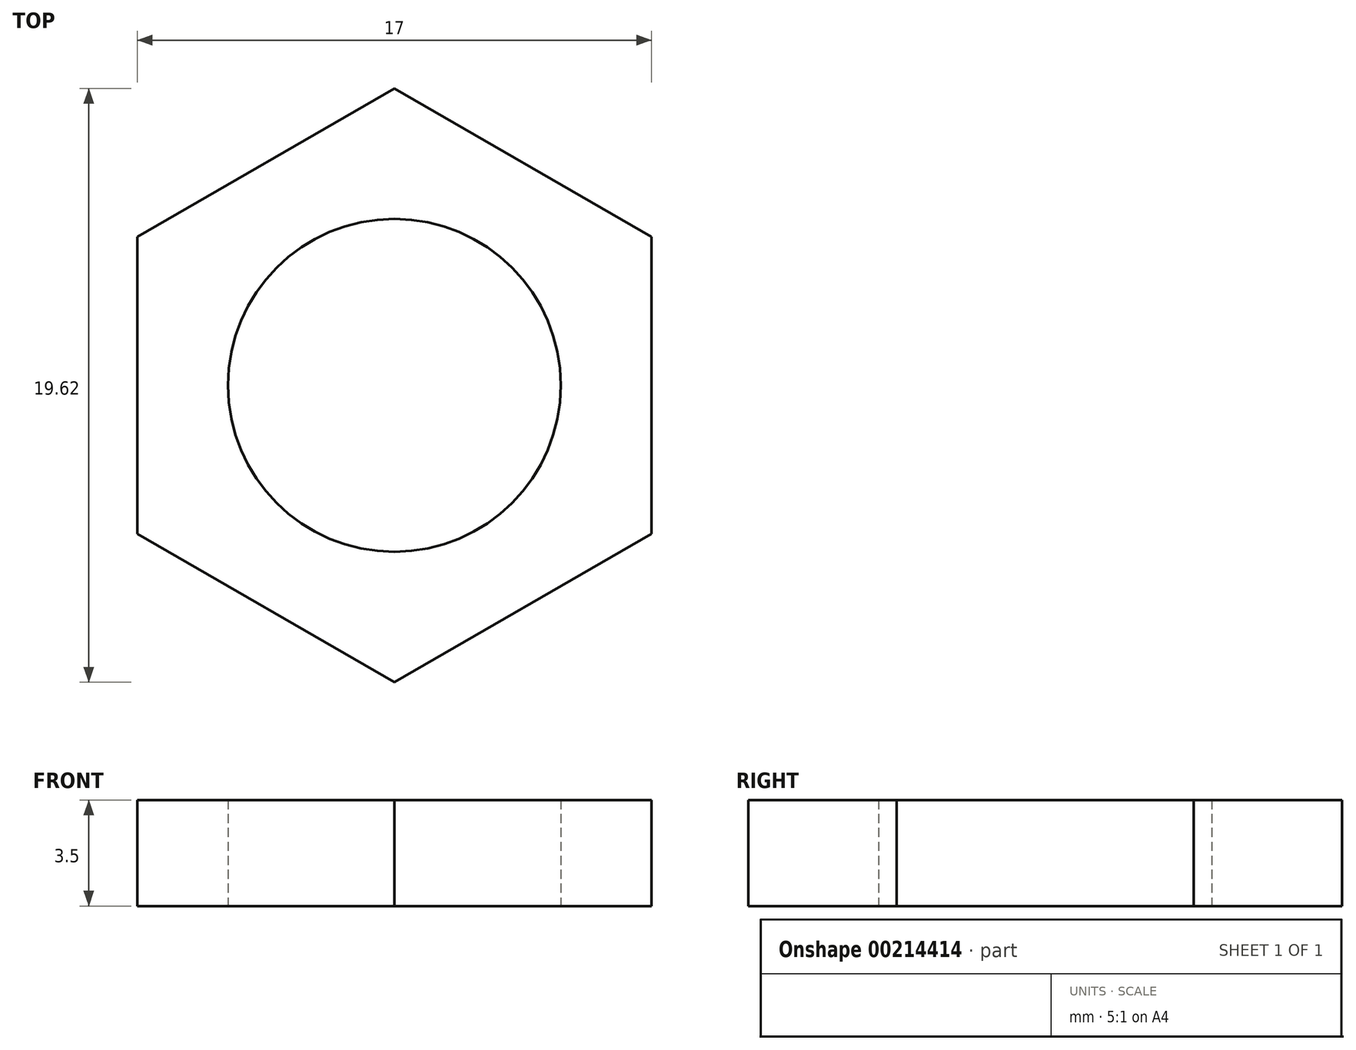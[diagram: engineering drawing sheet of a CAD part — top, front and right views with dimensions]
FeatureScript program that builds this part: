
annotation { "Feature Type Name" : "Feature", "Feature Type Description" : "" }
export const myFeature = defineFeature(function(context is Context, id is Id, definition is map)
    precondition{}
    {
        {
            var Q0;
            Q0=qCreatedBy(makeId("Top.planeOp"),FACE);
            var sketch = newSketch(context, id + "F0", { "sketchPlane" : qUnion([Q0])});
            skCircle(sketch, "E0.cCircle", {"center": v(0, 0) * mm, "radius": 8.5 * mm, "construction": true});
            skLineSegment(sketch, "E0.0", {"start": v(8.5, -4.9) * mm, "end": v(0, -9.81) * mm});
            skLineSegment(sketch, "E0.1", {"start": v(0, -9.81) * mm, "end": v(-8.5, -4.9) * mm});
            skLineSegment(sketch, "E0.2", {"start": v(-8.5, -4.9) * mm, "end": v(-8.5, 4.9) * mm});
            skLineSegment(sketch, "E0.3", {"start": v(-8.5, 4.9) * mm, "end": v(0, 9.81) * mm});
            skLineSegment(sketch, "E0.4", {"start": v(0, 9.81) * mm, "end": v(8.5, 4.9) * mm});
            skLineSegment(sketch, "E0.5", {"start": v(8.5, 4.9) * mm, "end": v(8.5, -4.9) * mm});
            skPoint(sketch, "E0.0.midPoint", {"position": v(4.25, -7.36) * mm});
            skLineSegment(sketch, "E1", {"start": v(0, 0) * mm, "end": v(0, 9.81) * mm, "construction": true});
            skCircle(sketch, "E2", {"center": v(0, 0) * mm, "radius": 5.5 * mm});
            skSolve(sketch);
        }
        {
            var Q0;
            Q0 = qSketchRegion(id + "F0", true);
            extrude(context, id + "F1", {"entities" : qUnion([Q0]), "depth" : 3.5 * mm});
        }
    });
